# Revit family: Overhead_Door-CHI-Counter_Shutter-6500
name_source: partatom
category: Specialty Equipment
units: mm (PartAtom-declared; Revit-internal decimal feet)

## family parameters
Always vertical = Yes
Classification Number = 23.30.60.14.17
Cut with Voids When Loaded = No
Enable Cutting in Views = No
Host = Wall
Maintain Annotation Orientation = No
Part Type = Normal
Room Calculation Point = No
Round Connector Dimension = Use Diameter
Shared = No

## types (5) — shared parameters
Assembly Code = B2030410
C Backroom = 0' - 10 1/2"
C Door Thickness = 0' - 0 5/16"
C Headroom = 1' - 1 1/2"
C Top Box Height = 0' - 10"
Default Elevation = 2' - 4"
Description = Roll-up Counter Shutter
Fire Rating = Contact Manufacturer for More Information
Keynote = 08 30 00
Manufacturer = C.H.I. Overhead Doors
Manufacturer Fax Number = 800-677-2650
Panel Thickness = 0' - 0 1/2"
Product Documentation Link = https://cdn2.hubspot.net
Product Page URL = https://www.chiohd.com
URL = https://www.chiohd.com
Version = 2021-v1.a
Warranty URL = https://www.chiohd.com

## per-type parameters (varying)
| type | Constraints | Material | Model | Panel Finish | Steel Gauge |
| Counter Shutter - 6522 - Gray - F1.5 Flat Slat | 1 | Steel - C.H.I Overhead Doors - Gray | 6522 | Steel - C.H.I Overhead Doors - F1.5 Flat Slat - Gray | 22 |
| Counter Shutter - 6566 - Stainless - F1.5 Flat Slat | 3 | Steel - C.H.I Overhead Doors - Stainless | 6566 | Steel - C.H.I Overhead Doors - F1.5 Flat Slat - Stainless | 22 |
| Counter Shutter - 6544 - Clear Anodized - F1.5 Flat Slat | 2 | Aluminum - C.H.I Overhead Doors - Clear Anodized | 6544 | Aluminum - C.H.I Overhead Doors - Flat Slat F1.5 - Clear Anodized | 16 |
| Counter Shutter - 6522 - White - F1.5 Flat Slat | 1 | Steel - C.H.I Overhead Doors - White | 6522 | Steel - C.H.I Overhead Doors - F1.5 Flat Slat - White | 22 |
| Counter Shutter - 6522 - Galvanized - F1.5 Flat Slat | 1 | Steel - C.H.I Overhead Doors - Unpainted Galvanized | 6522 | Steel - C.H.I Overhead Doors - F1.5 Flat Slat - Unpainted Galvanized | 22 |

## geometry (parser evidence)
native form markers: Sweep x7
no freeform markers — native parametric forms only
